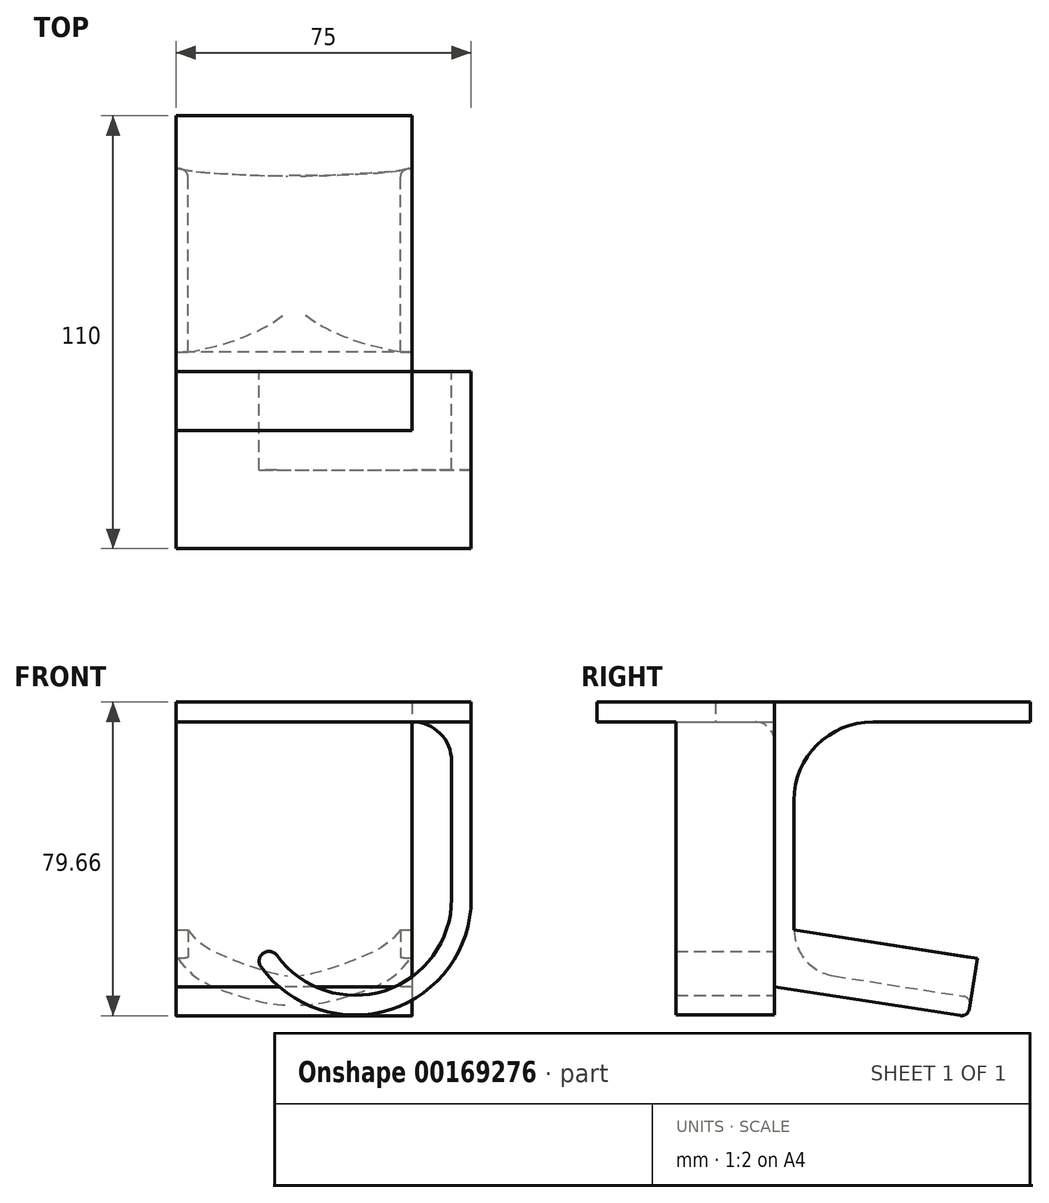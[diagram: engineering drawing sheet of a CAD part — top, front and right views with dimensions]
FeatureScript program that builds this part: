
annotation { "Feature Type Name" : "Feature", "Feature Type Description" : "" }
export const myFeature = defineFeature(function(context is Context, id is Id, definition is map)
    precondition{}
    {
        {
            var Q0;
            Q0=qCreatedBy(makeId("Right.planeOp"),FACE);
            var sketch = newSketch(context, id + "F0", { "sketchPlane" : qUnion([Q0])});
            skLineSegment(sketch, "E0", {"start": v(65, 0) * mm, "end": v(0, 0) * mm});
            skLineSegment(sketch, "E1", {"start": v(0, 0) * mm, "end": v(0, -72.28) * mm});
            skLineSegment(sketch, "E2", {"start": v(0, -72.28) * mm, "end": v(49.23, -79.94) * mm});
            skLineSegment(sketch, "E3.0", {"start": v(5, -68) * mm, "end": v(50, -75) * mm});
            skLineSegment(sketch, "E3.1", {"start": v(5, -5) * mm, "end": v(5, -68) * mm});
            skLineSegment(sketch, "E3.2", {"start": v(65, -5) * mm, "end": v(5, -5) * mm});
            skLineSegment(sketch, "E4", {"start": v(65, 0) * mm, "end": v(65, -5) * mm});
            skLineSegment(sketch, "E5", {"start": v(50, -75) * mm, "end": v(49.23, -79.94) * mm});
            skLineSegment(sketch, "E6", {"start": v(0, 0) * mm, "end": v(-15, 0) * mm});
            skLineSegment(sketch, "E7", {"start": v(-15, 0) * mm, "end": v(-15, -5) * mm});
            skLineSegment(sketch, "E8", {"start": v(-15, -5) * mm, "end": v(0, -5) * mm});
            skSolve(sketch);
        }
        {
            var Q0;
            Q0 = qSketchRegion(id + "F0", true);
            extrude(context, id + "F1", {"entities" : qUnion([Q0]), "depth" : 60 * mm});
        }
        {
            var Q0;
            Q0=makeQuery(id+"F1.opExtrude","SWEPT_FACE",FACE,{"disambiguationData":[OSD([sQuery(id+"F0.wireOp",EDGE,"E5")])]});
            var sketch = newSketch(context, id + "F2", { "sketchPlane" : qUnion([Q0])});
            skLineSegment(sketch, "E9", {"start": v(-31.68, -66.42) * mm, "end": v(-60, -66.42) * mm});
            skLineSegment(sketch, "E10", {"start": v(-60, -66.42) * mm, "end": v(-60, -56.42) * mm});
            skLineSegment(sketch, "E11", {"start": v(-60, -56.42) * mm, "end": v(-56.98, -56.42) * mm});
            skFitSpline(sketch, "E12", {"points": [v(-56.98, -56.42) * mm, v(-47.57, -62.71) * mm, v(-31.68, -66.42) * mm], "startDerivative": vector(17.17, -22.63) * mm, "endDerivative": vector(25.36, 0) * mm});
            skLineSegment(sketch, "E13", {"start": v(0, -66.42) * mm, "end": v(-30, -66.42) * mm});
            skLineSegment(sketch, "E14", {"start": v(-30, -66.42) * mm, "end": v(-30, -45.38) * mm});
            skFitSpline(sketch, "E15.MirrorCS", {"points": [v(-3.02, -56.42) * mm, v(-12.43, -62.71) * mm, v(-28.32, -66.42) * mm], "startDerivative": vector(-17.17, -22.63) * mm, "endDerivative": vector(-25.36, 0) * mm});
            skLineSegment(sketch, "E16.MirrorCS", {"start": v(0, -56.42) * mm, "end": v(-3.02, -56.42) * mm});
            skLineSegment(sketch, "E17.MirrorCS", {"start": v(0, -66.42) * mm, "end": v(0, -56.42) * mm});
            skLineSegment(sketch, "E18.MirrorCS", {"start": v(-28.32, -66.42) * mm, "end": v(0, -66.42) * mm});
            skSolve(sketch);
        }
        {
            var Q0;
            Q0 = qSketchRegion(id + "F2", true);
            var Q1;
            Q1=makeQuery(id+"F1.opExtrude","SWEPT_FACE",FACE,{"disambiguationData":[OSD([sQuery(id+"F0.wireOp",EDGE,"E3.1")])]});
            extrude(context, id + "F3", {"entities" : qUnion([Q0]), "operationType" : NewBodyOperationType.ADD, "oppositeDirection" : true, "endBoundEntityFace" : qUnion([Q1]), "depth" : 48.1 * mm});
        }
        {
            var Q0;
            Q0=makeQuery(id+"F1.opExtrude","SWEPT_EDGE",EDGE,{"disambiguationData":[OSD([sQuery(id+"F0.wireOp",EDGE,"E3.1"),sQuery(id+"F0.wireOp",EDGE,"E3.2")])]});
            fillet(context, id + "F4", {"entities" : qUnion([Q0]), "radius" : 20 * mm, "tangentPropagation" : true, "allowEdgeOverflow" : false});
        }
        {
            var Q0;
            Q0=makeQuery(id+"F1.opExtrude","SWEPT_EDGE",EDGE,{"disambiguationData":[OSD([sQuery(id+"F0.wireOp",EDGE,"E3.0"),sQuery(id+"F0.wireOp",EDGE,"E3.1")])]});
            fillet(context, id + "F5", {"entities" : qUnion([Q0]), "radius" : 12 * mm, "tangentPropagation" : true, "allowEdgeOverflow" : false});
        }
        {
            var Q0;
            Q0=makeQuery(id+"F1.opExtrude","SWEPT_EDGE",EDGE,{"disambiguationData":[OSD([sQuery(id+"F0.wireOp",EDGE,"E3.0"),sQuery(id+"F0.wireOp",EDGE,"E5")])]});
            var Q1;
            Q1=makeQuery(id+"F1.opExtrude","SWEPT_EDGE",EDGE,{"disambiguationData":[OSD([sQuery(id+"F0.wireOp",EDGE,"E2"),sQuery(id+"F0.wireOp",EDGE,"E5")])]});
            fillet(context, id + "F6", {"entities" : qUnion([Q0, Q1]), "radius" : 2 * mm, "tangentPropagation" : true, "allowEdgeOverflow" : false});
        }
        {
            var Q0;
            Q0=makeQuery(id+"F1.opExtrude","SWEPT_EDGE",EDGE,{"disambiguationData":[OSD([sQuery(id+"F0.wireOp",EDGE,"E1"),sQuery(id+"F0.wireOp",EDGE,"E8")])]});
            fillet(context, id + "F7", {"entities" : qUnion([Q0]), "radius" : 5 * mm, "tangentPropagation" : true, "allowEdgeOverflow" : false});
        }
        {
            var Q0;
            Q0=qCreatedBy(makeId("Front.planeOp"),FACE);
            var sketch = newSketch(context, id + "F8", { "sketchPlane" : qUnion([Q0])});
            skLineSegment(sketch, "E19", {"start": v(0, 0) * mm, "end": v(75, 0) * mm});
            skLineSegment(sketch, "E20", {"start": v(75, 0) * mm, "end": v(75, -50) * mm});
            skLineSegment(sketch, "E21", {"start": v(70, -50) * mm, "end": v(70, -5) * mm});
            skLineSegment(sketch, "E22", {"start": v(70, -5) * mm, "end": v(0, -5) * mm});
            skLineSegment(sketch, "E23", {"start": v(0, -5) * mm, "end": v(0, 0) * mm});
            skCircle(sketch, "E24", {"center": v(45.5, -50) * mm, "radius": 24.5 * mm});
            skCircle(sketch, "E25.0", {"center": v(45.5, -50) * mm, "radius": 29.5 * mm});
            skLineSegment(sketch, "E26", {"start": v(45.5, -50) * mm, "end": v(20.1, -65) * mm});
            skSolve(sketch);
        }
        {
            var Q0;
            Q0=makeQuery(id+"F8.imprint","IMPRINT",FACE,{"disambiguationData":[TD([[makeQuery(id+"F8.imprint","IMPRINT",EDGE,{"derivedFrom":sQuery(id+"F8.wireOp",EDGE,"E19")}),-1.0]])]});
            var Q1;
            {var subQ4=sQuery(id+"F8.wireOp",EDGE,"E21");var subQ6=sQuery(id+"F8.wireOp",EDGE,"E24");var subQ7=makeQuery(id+"F8.imprint","INTERSECT",VERTEX,{"derivedFrom":[subQ4,subQ6]});Q1=makeQuery(id+"F8.imprint","IMPRINT",FACE,{"disambiguationData":[TD([[makeQuery(id+"F8.imprint","IMPRINT",EDGE,{"disambiguationData":[TD([[subQ7,-1.0]])],"derivedFrom":subQ4}),-1.0]])]});}
            extrude(context, id + "F9", {"entities" : qUnion([Q0, Q1]), "depth" : 25 * mm});
        }
        {
            var Q0;
            Q0=makeQuery(id+"F9.opExtrude","CAP_FACE",FACE,{"disambiguationData":[OSD([sQuery(id+"F8.wireOp",EDGE,"E19"),sQuery(id+"F8.wireOp",EDGE,"E20"),sQuery(id+"F8.wireOp",EDGE,"E21"),sQuery(id+"F8.wireOp",EDGE,"E22"),sQuery(id+"F8.wireOp",EDGE,"E23"),sQuery(id+"F8.wireOp",EDGE,"E24"),sQuery(id+"F8.wireOp",EDGE,"E25.0"),sQuery(id+"F8.wireOp",EDGE,"E26")])],"isStart":false});
            var sketch = newSketch(context, id + "F10", { "sketchPlane" : qUnion([Q0])});
            skLineSegment(sketch, "E27.bottom", {"start": v(0, -5) * mm, "end": v(75, -5) * mm});
            skLineSegment(sketch, "E27.top", {"start": v(0, 0) * mm, "end": v(75, 0) * mm});
            skLineSegment(sketch, "E27.left", {"start": v(0, -5) * mm, "end": v(0, 0) * mm});
            skLineSegment(sketch, "E27.right", {"start": v(75, -5) * mm, "end": v(75, 0) * mm});
            skSolve(sketch);
        }
        {
            var Q0;
            Q0 = qSketchRegion(id + "F10", true);
            extrude(context, id + "F11", {"entities" : qUnion([Q0]), "operationType" : NewBodyOperationType.ADD, "depth" : 20 * mm});
        }
        {
            var Q0;
            Q0=makeQuery(id+"F11.opExtrude","CAP_EDGE",EDGE,{"disambiguationData":[OSD([sQuery(id+"F10.wireOp",EDGE,"E27.bottom")])],"isStart":true});
            var Q1;
            Q1=makeQuery(id+"F9.opExtrude","SWEPT_EDGE",EDGE,{"disambiguationData":[OSD([sQuery(id+"F8.wireOp",EDGE,"E21"),sQuery(id+"F8.wireOp",EDGE,"E22")])]});
            fillet(context, id + "F12", {"entities" : qUnion([Q0, Q1]), "radius" : 10 * mm, "tangentPropagation" : true, "allowEdgeOverflow" : false});
        }
        {
            var Q0;
            Q0=makeQuery(id+"F9.opExtrude","SWEPT_EDGE",EDGE,{"disambiguationData":[OSD([sQuery(id+"F8.wireOp",EDGE,"E24"),sQuery(id+"F8.wireOp",EDGE,"E26")])]});
            var Q1;
            Q1=makeQuery(id+"F9.opExtrude","SWEPT_EDGE",EDGE,{"disambiguationData":[OSD([sQuery(id+"F8.wireOp",EDGE,"E25.0"),sQuery(id+"F8.wireOp",EDGE,"E26")])]});
            fillet(context, id + "F13", {"entities" : qUnion([Q0, Q1]), "radius" : 2.5 * mm, "tangentPropagation" : true, "allowEdgeOverflow" : false});
        }
    });
